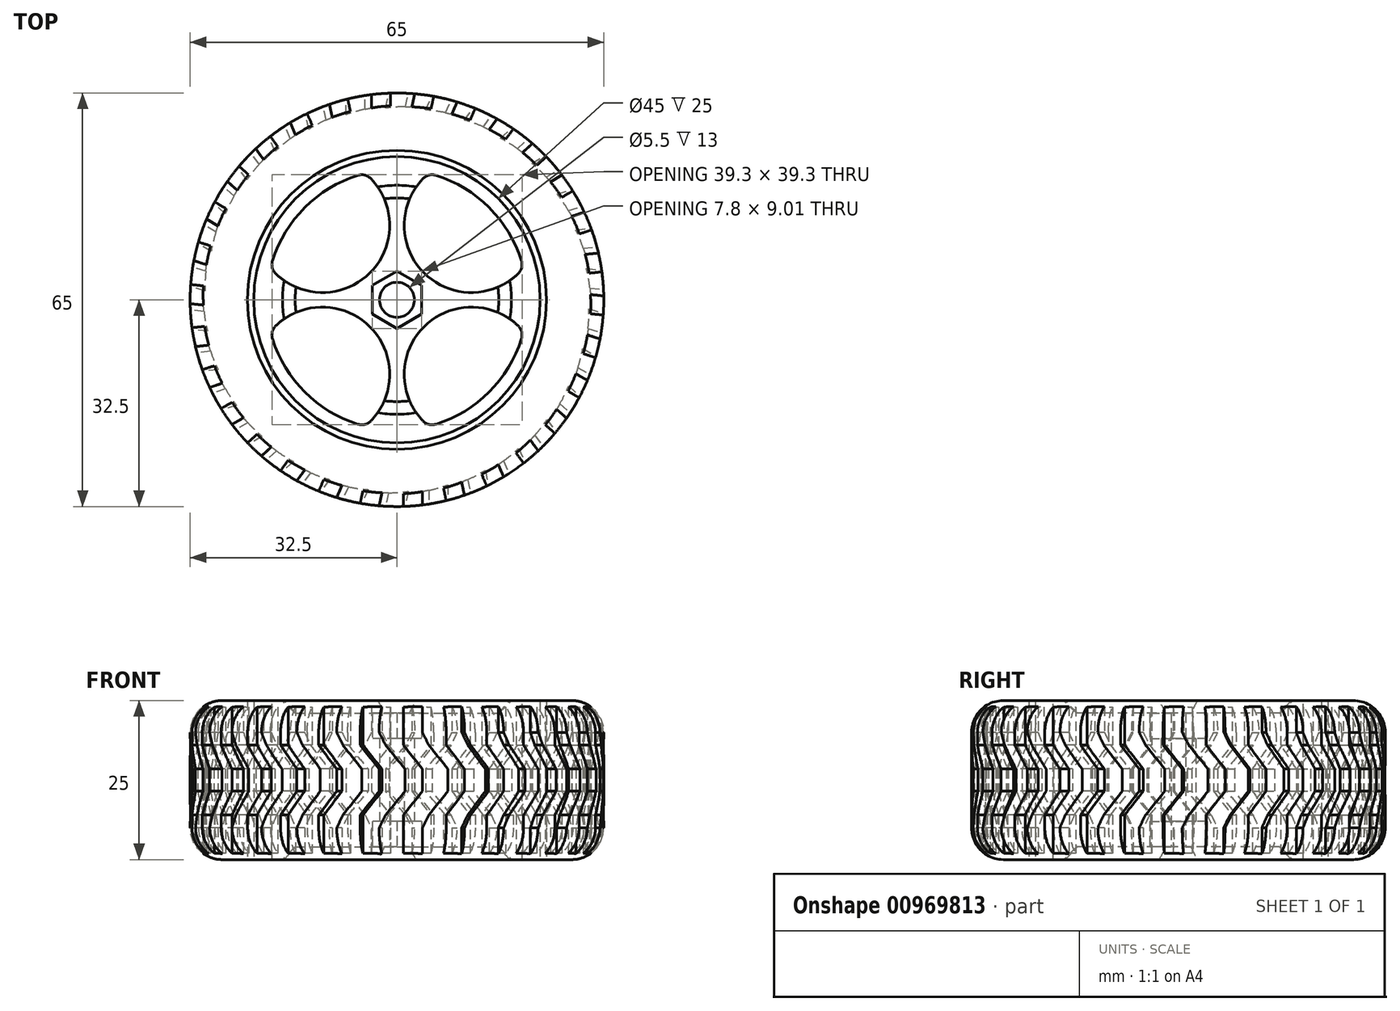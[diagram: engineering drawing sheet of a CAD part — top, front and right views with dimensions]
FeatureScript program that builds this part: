
annotation { "Feature Type Name" : "Feature", "Feature Type Description" : "" }
export const myFeature = defineFeature(function(context is Context, id is Id, definition is map)
    precondition{}
    {
        {
            assignVariable(context, id + "F0", {"name" : "Height", "anyValue" : 25});
        }
        {
            assignVariable(context, id + "F1", {"name" : "TreadCount", "anyValue" : 30});
        }
        {
            assignVariable(context, id + "F2", {"name" : "WheelDiameter", "anyValue" : 65});
        }
        {
            assignVariable(context, id + "F3", {"name" : "TireThickness", "anyValue" : 10});
        }
        {
            var Q0;
            Q0=qCreatedBy(makeId("Top.planeOp"),FACE);
            var sketch = newSketch(context, id + "F4", { "sketchPlane" : qUnion([Q0])});
            skCircle(sketch, "E0", {"center": v(0, 0) * mm, "radius": 32.5 * mm});
            skCircle(sketch, "E1", {"center": v(0, 0) * mm, "radius": 22.5 * mm});
            skCircle(sketch, "E2", {"center": v(0, 0) * mm, "radius": 2.75 * mm});
            skCircle(sketch, "E3", {"center": v(0, 0) * mm, "radius": 6 * mm});
            skCircle(sketch, "E4", {"center": v(0, 0) * mm, "radius": 23.5 * mm});
            skCircle(sketch, "E5", {"center": v(0, 0) * mm, "radius": 20.5 * mm});
            skArc(sketch, "E6", {"start": v(-19.88, 5) * mm, "mid": v(-4.24, 4.24) * mm, "end": v(-5, 19.88) * mm});
            skArc(sketch, "E7.MirrorCS", {"start": v(19.88, 5) * mm, "mid": v(4.24, 4.24) * mm, "end": v(5, 19.88) * mm});
            skArc(sketch, "E8.MirrorCS", {"start": v(19.88, -5) * mm, "mid": v(4.24, -4.24) * mm, "end": v(5, -19.88) * mm});
            skArc(sketch, "E9.MirrorCS", {"start": v(-19.88, -5) * mm, "mid": v(-4.24, -4.24) * mm, "end": v(-5, -19.88) * mm});
            skCircle(sketch, "E10.cCircle", {"center": v(0, 0) * mm, "radius": 3.9 * mm, "construction": true});
            skLineSegment(sketch, "E10.0", {"start": v(-3.9, -2.25) * mm, "end": v(-3.9, 2.25) * mm});
            skLineSegment(sketch, "E10.1", {"start": v(-3.9, 2.25) * mm, "end": v(0, 4.5) * mm});
            skLineSegment(sketch, "E10.2", {"start": v(0, 4.5) * mm, "end": v(3.9, 2.25) * mm});
            skLineSegment(sketch, "E10.3", {"start": v(3.9, 2.25) * mm, "end": v(3.9, -2.25) * mm});
            skLineSegment(sketch, "E10.4", {"start": v(3.9, -2.25) * mm, "end": v(0, -4.5) * mm});
            skLineSegment(sketch, "E10.5", {"start": v(0, -4.5) * mm, "end": v(-3.9, -2.25) * mm});
            skPoint(sketch, "E10.0.midPoint", {"position": v(-3.9, 0) * mm});
            skCircle(sketch, "E11", {"center": v(0, 0) * mm, "radius": 3 * mm});
            skSolve(sketch);
        }
        {
            var Q0;
            {var subQ0=sQuery(id+"F4.wireOp",EDGE,"E6");var subQ1=sQuery(id+"F4.wireOp",EDGE,"E3");var subQ2=makeQuery(id+"F4.imprint","INTERSECT",VERTEX,{"derivedFrom":[subQ1,subQ0]});Q0=makeQuery(id+"F4.imprint","IMPRINT",FACE,{"disambiguationData":[TD([[makeQuery(id+"F4.imprint","IMPRINT",EDGE,{"disambiguationData":[TD([[subQ2,-1.0]])],"derivedFrom":subQ1}),-1.0]])]});}
            var Q1;
            Q1=makeQuery(id+"F4.imprint","IMPRINT",FACE,{"disambiguationData":[TD([[makeQuery(id+"F4.imprint","IMPRINT",EDGE,{"derivedFrom":sQuery(id+"F4.wireOp",EDGE,"E1")}),1.0]])]});
            var Q2;
            Q2=makeQuery(id+"F4.imprint","IMPRINT",FACE,{"disambiguationData":[TD([[makeQuery(id+"F4.imprint","IMPRINT",EDGE,{"derivedFrom":sQuery(id+"F4.wireOp",EDGE,"E1")}),-1.0]])]});
            var Q3;
            {var subQ0=sQuery(id+"F4.wireOp",EDGE,"E6");var subQ1=sQuery(id+"F4.wireOp",EDGE,"E3");var subQ2=makeQuery(id+"F4.imprint","INTERSECT",VERTEX,{"derivedFrom":[subQ1,subQ0]});Q3=makeQuery(id+"F4.imprint","IMPRINT",FACE,{"disambiguationData":[TD([[makeQuery(id+"F4.imprint","IMPRINT",EDGE,{"disambiguationData":[TD([[subQ2,1.0]])],"derivedFrom":subQ1}),-1.0]])]});}
            var Q4;
            {var subQ0=sQuery(id+"F4.wireOp",EDGE,"E7.MirrorCS");var subQ1=sQuery(id+"F4.wireOp",EDGE,"E3");var subQ2=makeQuery(id+"F4.imprint","INTERSECT",VERTEX,{"derivedFrom":[subQ1,subQ0]});Q4=makeQuery(id+"F4.imprint","IMPRINT",FACE,{"disambiguationData":[TD([[makeQuery(id+"F4.imprint","IMPRINT",EDGE,{"disambiguationData":[TD([[subQ2,1.0]])],"derivedFrom":subQ1}),-1.0]])]});}
            var Q5;
            Q5=makeQuery(id+"F4.imprint","IMPRINT",FACE,{"disambiguationData":[TD([[makeQuery(id+"F4.imprint","IMPRINT",EDGE,{"derivedFrom":sQuery(id+"F4.wireOp",EDGE,"E10.0")}),1.0]])]});
            var Q6;
            {var subQ0=sQuery(id+"F4.wireOp",EDGE,"E9.MirrorCS");var subQ1=sQuery(id+"F4.wireOp",EDGE,"E3");var subQ2=makeQuery(id+"F4.imprint","INTERSECT",VERTEX,{"derivedFrom":[subQ1,subQ0]});Q6=makeQuery(id+"F4.imprint","IMPRINT",FACE,{"disambiguationData":[TD([[makeQuery(id+"F4.imprint","IMPRINT",EDGE,{"disambiguationData":[TD([[subQ2,-1.0]])],"derivedFrom":subQ1}),-1.0]])]});}
            var Q7;
            Q7=makeQuery(id+"F4.imprint","IMPRINT",FACE,{"disambiguationData":[TD([[makeQuery(id+"F4.imprint","IMPRINT",EDGE,{"derivedFrom":sQuery(id+"F4.wireOp",EDGE,"E10.0")}),-1.0]])]});
            extrude(context, id + "F5", {"entities" : qUnion([Q0, Q1, Q2, Q3, Q4, Q5, Q6, Q7]), "depth" : (getVariable(context, 'Height')) * mm, "offsetDistance" : 25 * mm});
        }
        {
            var Q0;
            Q0=makeQuery(id+"F4.imprint","IMPRINT",FACE,{"disambiguationData":[TD([[makeQuery(id+"F4.imprint","IMPRINT",EDGE,{"derivedFrom":sQuery(id+"F4.wireOp",EDGE,"E0")}),1.0]])]});
            var Q1;
            Q1=makeQuery(id+"F4.imprint","IMPRINT",FACE,{"disambiguationData":[TD([[makeQuery(id+"F4.imprint","IMPRINT",EDGE,{"derivedFrom":sQuery(id+"F4.wireOp",EDGE,"E1")}),-1.0]])]});
            extrude(context, id + "F6", {"entities" : qUnion([Q0, Q1]), "depth" : (getVariable(context, 'Height')) * mm, "offsetDistance" : 25 * mm});
        }
        {
            var Q0;
            Q0=makeQuery(id+"F4.imprint","IMPRINT",FACE,{"disambiguationData":[TD([[makeQuery(id+"F4.imprint","IMPRINT",EDGE,{"derivedFrom":sQuery(id+"F4.wireOp",EDGE,"E2")}),-1.0]])]});
            extrude(context, id + "F7", {"entities" : qUnion([Q0]), "operationType" : NewBodyOperationType.ADD, "depth" : (getVariable(context, 'Height') - 2) * mm, "offsetDistance" : 25 * mm, "hasSecondDirection" : true, "secondDirectionOppositeDirection" : false, "secondDirectionDepth" : 2 * mm});
        }
        {
            var Q0;
            Q0=makeQuery(id+"F5.opExtrude","CAP_EDGE",EDGE,{"disambiguationData":[OSD([sQuery(id+"F4.wireOp",EDGE,"E11")])],"isStart":true});
            var Q1;
            Q1=makeQuery(id+"F5.opExtrude","CAP_EDGE",EDGE,{"disambiguationData":[OSD([sQuery(id+"F4.wireOp",EDGE,"E11")])],"isStart":false});
            chamfer(context, id + "F8", {"entities" : qUnion([Q0, Q1]), "width" : 15 * mm, "tangentPropagation" : true});
        }
        {
            var Q0;
            Q0=qCreatedBy(makeId("Front.planeOp"),FACE);
            cPlane(context, id + "F9", {"entities" : qUnion([Q0]), "cplaneType" : CPlaneType.OFFSET, "offset" : (getVariable(context, 'WheelDiameter') / 2) * mm, "width" : 150 * mm, "height" : 150 * mm});
        }
        {
            var Q0;
            Q0=qCreatedBy(id+"F9.planeOp",FACE);
            var sketch = newSketch(context, id + "F10", { "sketchPlane" : qUnion([Q0])});
            skLineSegment(sketch, "E12", {"start": v(4, 25) * mm, "end": v(4, 20) * mm});
            skLineSegment(sketch, "E13", {"start": v(4, 20) * mm, "end": v(1, 20) * mm});
            skLineSegment(sketch, "E14", {"start": v(1, 20) * mm, "end": v(1, 25) * mm});
            skLineSegment(sketch, "E15", {"start": v(1, 25) * mm, "end": v(4, 25) * mm});
            skLineSegment(sketch, "E16", {"start": v(-35.1, 12.5) * mm, "end": v(42.93, 12.5) * mm, "construction": true});
            skLineSegment(sketch, "E17", {"start": v(1, 18) * mm, "end": v(4, 14.25) * mm});
            skLineSegment(sketch, "E18", {"start": v(4, 14.25) * mm, "end": v(8, 14.25) * mm});
            skLineSegment(sketch, "E19", {"start": v(8, 14.25) * mm, "end": v(5, 18) * mm});
            skLineSegment(sketch, "E20", {"start": v(5, 18) * mm, "end": v(1, 18) * mm});
            skLineSegment(sketch, "E21.MirrorCS", {"start": v(4, 10.75) * mm, "end": v(8, 10.75) * mm});
            skLineSegment(sketch, "E22.MirrorCS", {"start": v(8, 10.75) * mm, "end": v(5, 7) * mm});
            skLineSegment(sketch, "E23.MirrorCS", {"start": v(1, 7) * mm, "end": v(4, 10.75) * mm});
            skLineSegment(sketch, "E24.MirrorCS", {"start": v(5, 7) * mm, "end": v(1, 7) * mm});
            skLineSegment(sketch, "E25.MirrorCS", {"start": v(4, 5) * mm, "end": v(1, 5) * mm});
            skLineSegment(sketch, "E26.MirrorCS", {"start": v(4, 0) * mm, "end": v(4, 5) * mm});
            skLineSegment(sketch, "E27.MirrorCS", {"start": v(1, 5) * mm, "end": v(1, 0) * mm});
            skLineSegment(sketch, "E28.MirrorCS", {"start": v(1, 0) * mm, "end": v(4, 0) * mm});
            skLineSegment(sketch, "E29", {"start": v(1, 18) * mm, "end": v(1, 20) * mm});
            skLineSegment(sketch, "E30", {"start": v(5, 18) * mm, "end": v(4, 20) * mm});
            skLineSegment(sketch, "E31", {"start": v(4, 14.25) * mm, "end": v(4, 10.75) * mm});
            skLineSegment(sketch, "E32", {"start": v(8, 10.75) * mm, "end": v(8, 14.25) * mm});
            skLineSegment(sketch, "E33", {"start": v(1, 7) * mm, "end": v(1, 5) * mm});
            skLineSegment(sketch, "E34", {"start": v(4, 5) * mm, "end": v(5, 7) * mm});
            skSolve(sketch);
        }
        {
            var Q0;
            Q0=makeQuery(id+"F10.imprint","IMPRINT",FACE,{"disambiguationData":[TD([[makeQuery(id+"F10.imprint","IMPRINT",EDGE,{"derivedFrom":sQuery(id+"F10.wireOp",EDGE,"E25.MirrorCS")}),1.0]])]});
            var Q1;
            Q1=makeQuery(id+"F10.imprint","IMPRINT",FACE,{"disambiguationData":[TD([[makeQuery(id+"F10.imprint","IMPRINT",EDGE,{"derivedFrom":sQuery(id+"F10.wireOp",EDGE,"625af4f7-618a-4af6-95e0-114d10e541c610.MirrorCS")}),1.0]])]});
            var Q2;
            Q2=makeQuery(id+"F10.imprint","IMPRINT",FACE,{"disambiguationData":[TD([[makeQuery(id+"F10.imprint","IMPRINT",EDGE,{"derivedFrom":sQuery(id+"F10.wireOp",EDGE,"625af4f7-618a-4af6-95e0-114d10e541c61.MirrorCS")}),-1.0]])]});
            var Q3;
            Q3=makeQuery(id+"F10.imprint","IMPRINT",FACE,{"disambiguationData":[TD([[makeQuery(id+"F10.imprint","IMPRINT",EDGE,{"derivedFrom":sQuery(id+"F10.wireOp",EDGE,"625af4f7-618a-4af6-95e0-114d10e541c60.MirrorCS")}),-1.0]])]});
            var Q4;
            Q4=makeQuery(id+"F10.imprint","IMPRINT",FACE,{"disambiguationData":[TD([[makeQuery(id+"F10.imprint","IMPRINT",EDGE,{"derivedFrom":sQuery(id+"F10.wireOp",EDGE,"E18")}),-1.0]])]});
            var Q5;
            Q5=makeQuery(id+"F10.imprint","IMPRINT",FACE,{"disambiguationData":[TD([[makeQuery(id+"F10.imprint","IMPRINT",EDGE,{"derivedFrom":sQuery(id+"F10.wireOp",EDGE,"E12")}),-1.0]])]});
            var Q6;
            Q6=makeQuery(id+"F10.imprint","IMPRINT",FACE,{"disambiguationData":[TD([[makeQuery(id+"F10.imprint","IMPRINT",EDGE,{"derivedFrom":sQuery(id+"F10.wireOp",EDGE,"E13")}),1.0]])]});
            var Q7;
            Q7=makeQuery(id+"F10.imprint","IMPRINT",FACE,{"disambiguationData":[TD([[makeQuery(id+"F10.imprint","IMPRINT",EDGE,{"derivedFrom":sQuery(id+"F10.wireOp",EDGE,"625af4f7-618a-4af6-95e0-114d10e541c62.MirrorCS")}),-1.0]])]});
            var Q8;
            Q8=makeQuery(id+"F10.imprint","IMPRINT",FACE,{"disambiguationData":[TD([[makeQuery(id+"F10.imprint","IMPRINT",EDGE,{"derivedFrom":sQuery(id+"F10.wireOp",EDGE,"E21.MirrorCS")}),-1.0]])]});
            var Q9;
            Q9=makeQuery(id+"F10.imprint","IMPRINT",FACE,{"disambiguationData":[TD([[makeQuery(id+"F10.imprint","IMPRINT",EDGE,{"derivedFrom":sQuery(id+"F10.wireOp",EDGE,"E17")}),1.0]])]});
            var Q10;
            Q10=makeQuery(id+"F10.imprint","IMPRINT",FACE,{"disambiguationData":[TD([[makeQuery(id+"F10.imprint","IMPRINT",EDGE,{"derivedFrom":sQuery(id+"F10.wireOp",EDGE,"625af4f7-618a-4af6-95e0-114d10e541c68.MirrorCS")}),1.0]])]});
            var Q11;
            Q11=makeQuery(id+"F10.imprint","IMPRINT",FACE,{"disambiguationData":[TD([[makeQuery(id+"F10.imprint","IMPRINT",EDGE,{"derivedFrom":sQuery(id+"F10.wireOp",EDGE,"625af4f7-618a-4af6-95e0-114d10e541c66.MirrorCS")}),-1.0]])]});
            var Q12;
            Q12=makeQuery(id+"F10.imprint","IMPRINT",FACE,{"disambiguationData":[TD([[makeQuery(id+"F10.imprint","IMPRINT",EDGE,{"derivedFrom":sQuery(id+"F10.wireOp",EDGE,"625af4f7-618a-4af6-95e0-114d10e541c69.MirrorCS")}),-1.0]])]});
            var Q13;
            Q13=makeQuery(id+"F10.imprint","IMPRINT",FACE,{"disambiguationData":[TD([[makeQuery(id+"F10.imprint","IMPRINT",EDGE,{"derivedFrom":sQuery(id+"F10.wireOp",EDGE,"E24.MirrorCS")}),1.0]])]});
            var Q14;
            Q14=makeQuery(id+"F10.imprint","IMPRINT",FACE,{"disambiguationData":[TD([[makeQuery(id+"F10.imprint","IMPRINT",EDGE,{"derivedFrom":sQuery(id+"F10.wireOp",EDGE,"80671f75-de75-40dc-9725-3982954ffb580.MirrorCS")}),1.0]])]});
            var Q15;
            Q15=makeQuery(id+"F10.imprint","IMPRINT",FACE,{"disambiguationData":[TD([[makeQuery(id+"F10.imprint","IMPRINT",EDGE,{"derivedFrom":sQuery(id+"F10.wireOp",EDGE,"801fb4e2-fb68-4d74-9dd2-7f50cddcc5e40.MirrorCS")}),1.0]])]});
            var Q16;
            Q16=makeQuery(id+"F10.imprint","IMPRINT",FACE,{"disambiguationData":[TD([[makeQuery(id+"F10.imprint","IMPRINT",EDGE,{"derivedFrom":sQuery(id+"F10.wireOp",EDGE,"YH6J1Eje-LX5N-8zG1-BsBA-wbV9ktKcAqs1.bottom")}),-1.0]])]});
            var Q17;
            Q17=makeQuery(id+"F10.imprint","IMPRINT",FACE,{"disambiguationData":[TD([[makeQuery(id+"F10.imprint","IMPRINT",EDGE,{"derivedFrom":sQuery(id+"F10.wireOp",EDGE,"1a49f7d1-5964-4074-8dd1-1fce4bc8db700.MirrorCS")}),1.0]])]});
            var Q18;
            Q18=makeQuery(id+"F5.opExtrude","SWEPT_FACE",FACE,{"disambiguationData":[OSD([sQuery(id+"F4.wireOp",EDGE,"E4")])]});
            extrude(context, id + "F11", {"entities" : qUnion([Q0, Q1, Q2, Q3, Q4, Q5, Q6, Q7, Q8, Q9, Q10, Q11, Q12, Q13, Q14, Q15, Q16, Q17]), "endBound" : BoundingType.UP_TO_SURFACE, "oppositeDirection" : true, "depth" : 2 * mm, "endBoundEntityFace" : qUnion([Q18]), "hasOffset" : true, "offsetDistance" : (getVariable(context, 'TireThickness') - 3) * mm});
        }
        {
            var Q0;
            {var subQ0=sQuery(id+"F4.wireOp",EDGE,"E6");var subQ1=sQuery(id+"F4.wireOp",EDGE,"E5");Q0=makeQuery(id+"F5.opExtrude","SWEPT_EDGE",EDGE,{"disambiguationData":[OSD([subQ1,subQ0]),TDD([makeQuery(id+"F4.imprint","INTERSECT",VERTEX,{"disambiguationData":[OD(0.0)],"derivedFrom":[subQ1,subQ0]})])]});}
            var Q1;
            {var subQ0=sQuery(id+"F4.wireOp",EDGE,"E6");var subQ1=sQuery(id+"F4.wireOp",EDGE,"E5");Q1=makeQuery(id+"F5.opExtrude","SWEPT_EDGE",EDGE,{"disambiguationData":[OSD([subQ1,subQ0]),TDD([makeQuery(id+"F4.imprint","INTERSECT",VERTEX,{"disambiguationData":[OD(1.0)],"derivedFrom":[subQ1,subQ0]})])]});}
            var Q2;
            {var subQ0=sQuery(id+"F4.wireOp",EDGE,"E9.MirrorCS");var subQ1=sQuery(id+"F4.wireOp",EDGE,"E5");Q2=makeQuery(id+"F5.opExtrude","SWEPT_EDGE",EDGE,{"disambiguationData":[OSD([subQ1,subQ0]),TDD([makeQuery(id+"F4.imprint","INTERSECT",VERTEX,{"disambiguationData":[OD(1.0)],"derivedFrom":[subQ1,subQ0]})])]});}
            var Q3;
            {var subQ0=sQuery(id+"F4.wireOp",EDGE,"E9.MirrorCS");var subQ1=sQuery(id+"F4.wireOp",EDGE,"E5");Q3=makeQuery(id+"F5.opExtrude","SWEPT_EDGE",EDGE,{"disambiguationData":[OSD([subQ1,subQ0]),TDD([makeQuery(id+"F4.imprint","INTERSECT",VERTEX,{"disambiguationData":[OD(0.0)],"derivedFrom":[subQ1,subQ0]})])]});}
            var Q4;
            {var subQ0=sQuery(id+"F4.wireOp",EDGE,"E8.MirrorCS");var subQ1=sQuery(id+"F4.wireOp",EDGE,"E5");Q4=makeQuery(id+"F5.opExtrude","SWEPT_EDGE",EDGE,{"disambiguationData":[OSD([subQ1,subQ0]),TDD([makeQuery(id+"F4.imprint","INTERSECT",VERTEX,{"disambiguationData":[OD(1.0)],"derivedFrom":[subQ1,subQ0]})])]});}
            var Q5;
            {var subQ0=sQuery(id+"F4.wireOp",EDGE,"E8.MirrorCS");var subQ1=sQuery(id+"F4.wireOp",EDGE,"E5");Q5=makeQuery(id+"F5.opExtrude","SWEPT_EDGE",EDGE,{"disambiguationData":[OSD([subQ1,subQ0]),TDD([makeQuery(id+"F4.imprint","INTERSECT",VERTEX,{"disambiguationData":[OD(0.0)],"derivedFrom":[subQ1,subQ0]})])]});}
            var Q6;
            {var subQ0=sQuery(id+"F4.wireOp",EDGE,"E7.MirrorCS");var subQ1=sQuery(id+"F4.wireOp",EDGE,"E5");Q6=makeQuery(id+"F5.opExtrude","SWEPT_EDGE",EDGE,{"disambiguationData":[OSD([subQ1,subQ0]),TDD([makeQuery(id+"F4.imprint","INTERSECT",VERTEX,{"disambiguationData":[OD(0.0)],"derivedFrom":[subQ1,subQ0]})])]});}
            var Q7;
            {var subQ0=sQuery(id+"F4.wireOp",EDGE,"E7.MirrorCS");var subQ1=sQuery(id+"F4.wireOp",EDGE,"E5");Q7=makeQuery(id+"F5.opExtrude","SWEPT_EDGE",EDGE,{"disambiguationData":[OSD([subQ1,subQ0]),TDD([makeQuery(id+"F4.imprint","INTERSECT",VERTEX,{"disambiguationData":[OD(1.0)],"derivedFrom":[subQ1,subQ0]})])]});}
            fillet(context, id + "F12", {"entities" : qUnion([Q0, Q1, Q2, Q3, Q4, Q5, Q6, Q7]), "radius" : 2 * mm, "tangentPropagation" : true, "allowEdgeOverflow" : false});
        }
        {
            var Q0;
            Q0=makeQuery(id+"F6.opExtrude","CAP_EDGE",EDGE,{"disambiguationData":[OSD([sQuery(id+"F4.wireOp",EDGE,"E0")])],"isStart":false});
            var Q1;
            Q1=makeQuery(id+"F6.opExtrude","CAP_EDGE",EDGE,{"disambiguationData":[OSD([sQuery(id+"F4.wireOp",EDGE,"E0")])],"isStart":true});
            fillet(context, id + "F13", {"entities" : qUnion([Q0, Q1]), "radius" : 5 * mm, "tangentPropagation" : true, "allowEdgeOverflow" : false});
        }
        {
            var Q0;
            Q0=makeQuery(id+"F11.opExtrude","SWEPT_BODY",BODY,{"disambiguationData":[OSD([sQuery(id+"F10.wireOp",EDGE,"E12"),sQuery(id+"F10.wireOp",EDGE,"E13"),sQuery(id+"F10.wireOp",EDGE,"E14"),sQuery(id+"F10.wireOp",EDGE,"E15")])]});
            var Q1;
            Q1=makeQuery(id+"F11.opExtrude","SWEPT_BODY",BODY,{"disambiguationData":[OSD([sQuery(id+"F10.wireOp",EDGE,"E17"),sQuery(id+"F10.wireOp",EDGE,"E18"),sQuery(id+"F10.wireOp",EDGE,"E19"),sQuery(id+"F10.wireOp",EDGE,"E20")])]});
            var Q2;
            Q2=makeQuery(id+"F11.opExtrude","SWEPT_BODY",BODY,{"disambiguationData":[OSD([sQuery(id+"F10.wireOp",EDGE,"E21.MirrorCS"),sQuery(id+"F10.wireOp",EDGE,"E22.MirrorCS"),sQuery(id+"F10.wireOp",EDGE,"E23.MirrorCS"),sQuery(id+"F10.wireOp",EDGE,"E24.MirrorCS")])]});
            var Q3;
            Q3=makeQuery(id+"F11.opExtrude","SWEPT_BODY",BODY,{"disambiguationData":[OSD([sQuery(id+"F10.wireOp",EDGE,"E25.MirrorCS"),sQuery(id+"F10.wireOp",EDGE,"E26.MirrorCS"),sQuery(id+"F10.wireOp",EDGE,"E27.MirrorCS"),sQuery(id+"F10.wireOp",EDGE,"E28.MirrorCS")])]});
            var Q4;
            Q4=makeQuery(id+"F11.opExtrude","SWEPT_BODY",BODY,{"disambiguationData":[OSD([sQuery(id+"F10.wireOp",EDGE,"80671f75-de75-40dc-9725-3982954ffb580.MirrorCS"),sQuery(id+"F10.wireOp",EDGE,"021eff91-bfe0-453e-989a-a67f698f9a2d0.MirrorCS"),sQuery(id+"F10.wireOp",EDGE,"d59b37d8-7269-4f79-a061-b74ca02b38580.MirrorCS"),sQuery(id+"F10.wireOp",EDGE,"b473a42d-66c1-4af3-9827-93953d6ccba30.MirrorCS")])]});
            var Q5;
            Q5=makeQuery(id+"F11.opExtrude","SWEPT_BODY",BODY,{"disambiguationData":[OSD([sQuery(id+"F10.wireOp",EDGE,"801fb4e2-fb68-4d74-9dd2-7f50cddcc5e40.MirrorCS"),sQuery(id+"F10.wireOp",EDGE,"c9f9deed-9c66-4708-8608-04be0700cbfe0.MirrorCS"),sQuery(id+"F10.wireOp",EDGE,"8e74ccbd-02c0-4367-97e9-8b461c46e9fd0.MirrorCS"),sQuery(id+"F10.wireOp",EDGE,"80d523ca-8f21-47f3-9288-e6795d85213a0.MirrorCS")])]});
            var Q6;
            Q6=makeQuery(id+"F11.opExtrude","SWEPT_BODY",BODY,{"disambiguationData":[OSD([sQuery(id+"F10.wireOp",EDGE,"YH6J1Eje-LX5N-8zG1-BsBA-wbV9ktKcAqs1.bottom"),sQuery(id+"F10.wireOp",EDGE,"YH6J1Eje-LX5N-8zG1-BsBA-wbV9ktKcAqs1.top"),sQuery(id+"F10.wireOp",EDGE,"YH6J1Eje-LX5N-8zG1-BsBA-wbV9ktKcAqs1.left"),sQuery(id+"F10.wireOp",EDGE,"YH6J1Eje-LX5N-8zG1-BsBA-wbV9ktKcAqs1.right")])]});
            var Q7;
            Q7=makeQuery(id+"F11.opExtrude","SWEPT_BODY",BODY,{"disambiguationData":[OSD([sQuery(id+"F10.wireOp",EDGE,"1a49f7d1-5964-4074-8dd1-1fce4bc8db700.MirrorCS"),sQuery(id+"F10.wireOp",EDGE,"1175bd12-8c3b-4887-9aee-3702b65b68e10.MirrorCS"),sQuery(id+"F10.wireOp",EDGE,"19226e74-338a-4957-8c3c-efd0ca807d6a0.MirrorCS"),sQuery(id+"F10.wireOp",EDGE,"90379b1c-c5db-45ec-8afd-aa151c76bcad0.MirrorCS")])]});
            var Q8;
            Q8=makeQuery(id+"F7.opExtrude","CAP_EDGE",EDGE,{"disambiguationData":[OSD([sQuery(id+"F4.wireOp",EDGE,"E2")])],"isStart":false});
            circularPattern(context, id + "F14", {"operationType" : NewBodyOperationType.REMOVE, "entities" : qUnion([Q0, Q1, Q2, Q3, Q4, Q5, Q6, Q7]), "axis" : qUnion([Q8]), "angle" : 360 * degree, "instanceCount" : getVariable(context, 'TreadCount'), "equalSpace" : true});
        }
        {
            var Q0;
            Q0=makeQuery(id+"F4.imprint","IMPRINT",FACE,{"disambiguationData":[TD([[makeQuery(id+"F4.imprint","IMPRINT",EDGE,{"derivedFrom":sQuery(id+"F4.wireOp",EDGE,"E10.0")}),-1.0]])]});
            var Q1;
            Q1=makeQuery(id+"F4.imprint","IMPRINT",FACE,{"disambiguationData":[TD([[makeQuery(id+"F4.imprint","IMPRINT",EDGE,{"derivedFrom":sQuery(id+"F4.wireOp",EDGE,"E2")}),-1.0]])]});
            var Q2;
            Q2=makeQuery(id+"F4.imprint","IMPRINT",FACE,{"disambiguationData":[TD([[makeQuery(id+"F4.imprint","IMPRINT",EDGE,{"derivedFrom":sQuery(id+"F4.wireOp",EDGE,"E2")}),1.0]])]});
            extrude(context, id + "F15", {"entities" : qUnion([Q0, Q1, Q2]), "operationType" : NewBodyOperationType.REMOVE, "depth" : 6 * mm, "offsetDistance" : 25 * mm});
        }
        {
            var Q0;
            Q0=makeQuery(id+"F4.imprint","IMPRINT",FACE,{"disambiguationData":[TD([[makeQuery(id+"F4.imprint","IMPRINT",EDGE,{"derivedFrom":sQuery(id+"F4.wireOp",EDGE,"E10.0")}),-1.0]])]});
            var Q1;
            Q1=makeQuery(id+"F4.imprint","IMPRINT",FACE,{"disambiguationData":[TD([[makeQuery(id+"F4.imprint","IMPRINT",EDGE,{"derivedFrom":sQuery(id+"F4.wireOp",EDGE,"E2")}),-1.0]])]});
            extrude(context, id + "F16", {"entities" : qUnion([Q0, Q1]), "operationType" : NewBodyOperationType.REMOVE, "depth" : (getVariable(context, 'Height')) * mm, "offsetDistance" : 25 * mm, "hasSecondDirection" : true, "secondDirectionOppositeDirection" : false, "secondDirectionDepth" : (getVariable(context, 'Height') - 6) * mm});
        }
    });
